# Revit family: NRG304B
name_source: partatom
category: Lighting Fixtures
revit_build: Autodesk Revit Architecture 2012 (Build: 20110309_2315(x64)
units: mm (PartAtom-declared; Revit-internal decimal feet)

## types (1)
- NRG 304B
    Backbox = Dark Bronze
    Color Filter = 16777215
    Default Elevation = 48.000"
    Description = Entry or single story perimeter lighting for safety, security and identity. Use on commercial buildings, shopping centers, schools, apartment complexes as well as non-supervised vandal prone applications.
    Dimming Lamp Color Temperature Shift = <None>
    Glass = Glass
    Glass Pattern = Glass 2
    Lamp = CFL,HPS,PSMH
    Light Source Symbol Size = 4.500"
    Manufacturer = Hubbell Outdoor Lighting
    Manufacturer Fax = (864)-678-1415
    Model = NRG 304B
    Mounting = Ceiling Or Wall Mount
    Product Documentation Link = http://www.hubbelloutdoor.com
    Product Page URL = http://www.hubbelloutdoor.com
    URL = http://www.hubbelloutdoor.com
    Wattage Comments = 42-70W

## geometry (parser evidence)
native form markers: Blend x2, Sweep x1
no freeform markers — native parametric forms only
